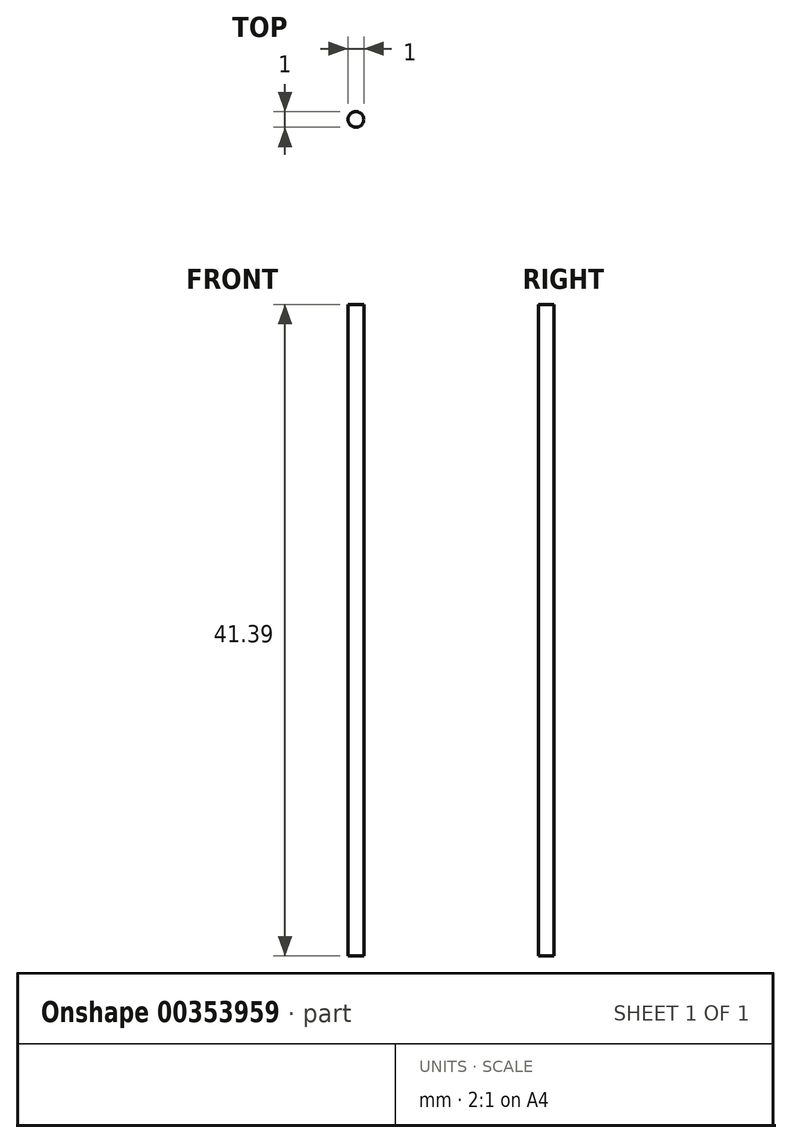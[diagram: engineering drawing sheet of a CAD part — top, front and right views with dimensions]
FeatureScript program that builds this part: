
annotation { "Feature Type Name" : "Feature", "Feature Type Description" : "" }
export const myFeature = defineFeature(function(context is Context, id is Id, definition is map)
    precondition{}
    {
        {
            var Q0;
            Q0=qCreatedBy(makeId("Top.planeOp"),FACE);
            var sketch = newSketch(context, id + "F0", { "sketchPlane" : qUnion([Q0])});
            skCircle(sketch, "E0", {"center": v(0, 0) * mm, "radius": 0.5 * mm});
            skSolve(sketch);
        }
        {
            var Q0;
            Q0=makeQuery(id+"F0.imprint","IMPRINT",FACE,{"disambiguationData":[TD([[makeQuery(id+"F0.imprint","IMPRINT",EDGE,{"derivedFrom":sQuery(id+"F0.wireOp",EDGE,"E0")}),1.0]])]});
            extrude(context, id + "F1", {"entities" : qUnion([Q0]), "depth" : 41.4 * mm});
        }
    });
